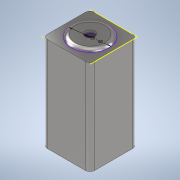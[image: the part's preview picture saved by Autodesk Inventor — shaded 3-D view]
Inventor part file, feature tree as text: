
AUTODESK INVENTOR PART (.ipt)
format: ipt  version: 2022 (Build 260153000, 153)  size: 130,048 bytes
history: native  units: in
note: dims shown in document units (in); Inventor stores cm internally (conversion verified against a paired STEP export)
features: extrude x3, sketch x2, fillet x2
ambient origin geometry x8: Origin, YZ Plane, XZ Plane, XY Plane, X Axis, Y Axis, Z Axis, Center Point
bodies: Solid1 (feature_tree)
feature tree (7):
  extrude  "Extrusion1"  Depth=3.937in
  sketch  "Sketch2"  dims[d2=7.874in d3=0.0in d4=0.7874in d5=3.1496in d6=6.8898in d7=0.0in d8=0.1969in d9=0.0in d10=0.3937in d11=0.3937in]
  extrude  "Extrusion2"  Depth=0.3937in
  extrude  "Extrusion3"  Depth=0.3937in
  fillet  "Fillet1"  Radius=6.8898in
  fillet  "Fillet2"  Radius=0.1969in
  sketch  "Sketch1"  dims[d0=3.937in d1=3.937in]
